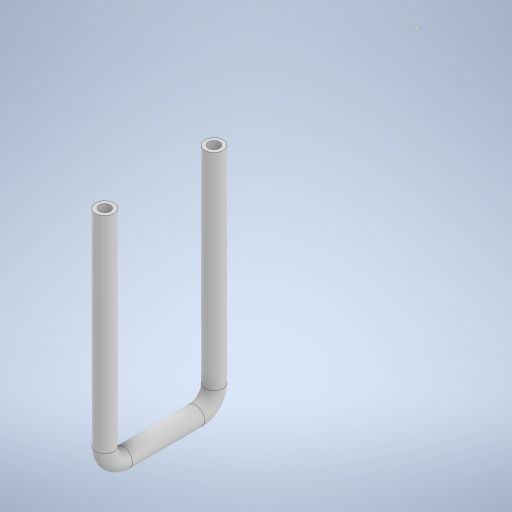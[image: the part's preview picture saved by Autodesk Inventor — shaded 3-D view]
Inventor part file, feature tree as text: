
AUTODESK INVENTOR PART (.ipt)
format: ipt  version: 2024 (Build 280153000, 153)  size: 283,648 bytes
history: native  units: in
note: dims shown in document units (in); Inventor stores cm internally (conversion verified against a paired STEP export)
features: sketch x4, other x2, extrude x1, plane x1
ambient origin geometry x8: Origin, YZ Plane, XZ Plane, XY Plane, X Axis, Y Axis, Z Axis, Center Point
bodies: Solid1 (feature_tree)
feature tree (8):
  extrude  "Extrusion1"  Depth=0.9843in
  plane  "Work Plane2"
  other  "Bend Part1"
  other  "Bend Part2"
  sketch  "Sketch5"  dims[d8=11.811in d9=0.5in d10=90.0deg d11=11.811in d12=0.5in d13=90.0deg]
  sketch  "Sketch1"  dims[d0=0.5906in d1=0.9843in]
  sketch  "Sketch3"  dims[d2=27.4803in d3=0.0in]
  sketch  "Sketch4"  dims[d7=11.811in]
